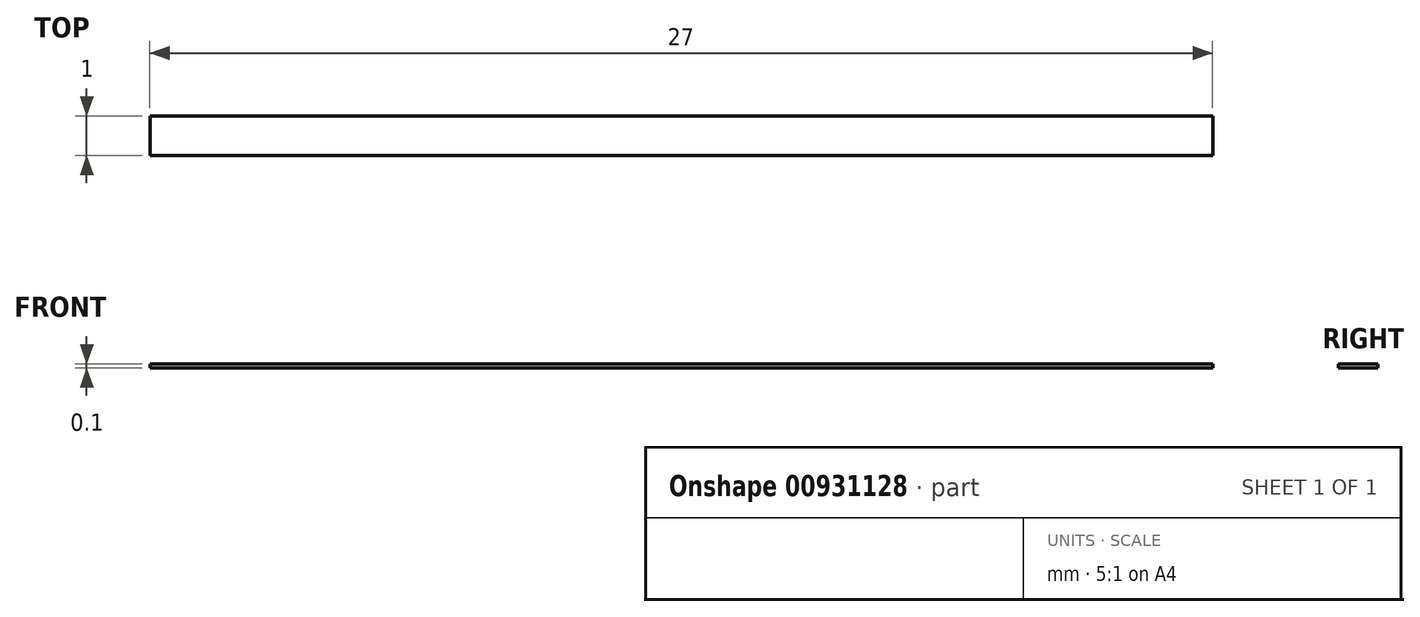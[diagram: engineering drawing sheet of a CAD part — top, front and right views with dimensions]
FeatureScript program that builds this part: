
annotation { "Feature Type Name" : "Feature", "Feature Type Description" : "" }
export const myFeature = defineFeature(function(context is Context, id is Id, definition is map)
    precondition{}
    {
        {
            var Q0;
            Q0=qCreatedBy(makeId("Front.planeOp"),FACE);
            var sketch = newSketch(context, id + "F0", { "sketchPlane" : qUnion([Q0])});
            skLineSegment(sketch, "E0.bottom", {"start": v(-60.37, 21.01) * mm, "end": v(-33.37, 21.01) * mm});
            skLineSegment(sketch, "E0.top", {"start": v(-60.37, 20.91) * mm, "end": v(-33.37, 20.91) * mm});
            skLineSegment(sketch, "E0.left", {"start": v(-60.37, 21.01) * mm, "end": v(-60.37, 20.91) * mm});
            skLineSegment(sketch, "E0.right", {"start": v(-33.37, 21.01) * mm, "end": v(-33.37, 20.91) * mm});
            skSolve(sketch);
        }
        {
            var Q0;
            Q0=makeQuery(id+"F0.imprint","IMPRINT",FACE,{"disambiguationData":[TD([[makeQuery(id+"F0.imprint","IMPRINT",EDGE,{"derivedFrom":sQuery(id+"F0.wireOp",EDGE,"E0.bottom")}),-1.0]])]});
            extrude(context, id + "F1", {"entities" : qUnion([Q0]), "depth" : 1 * mm, "offsetDistance" : 25 * mm});
        }
    });
